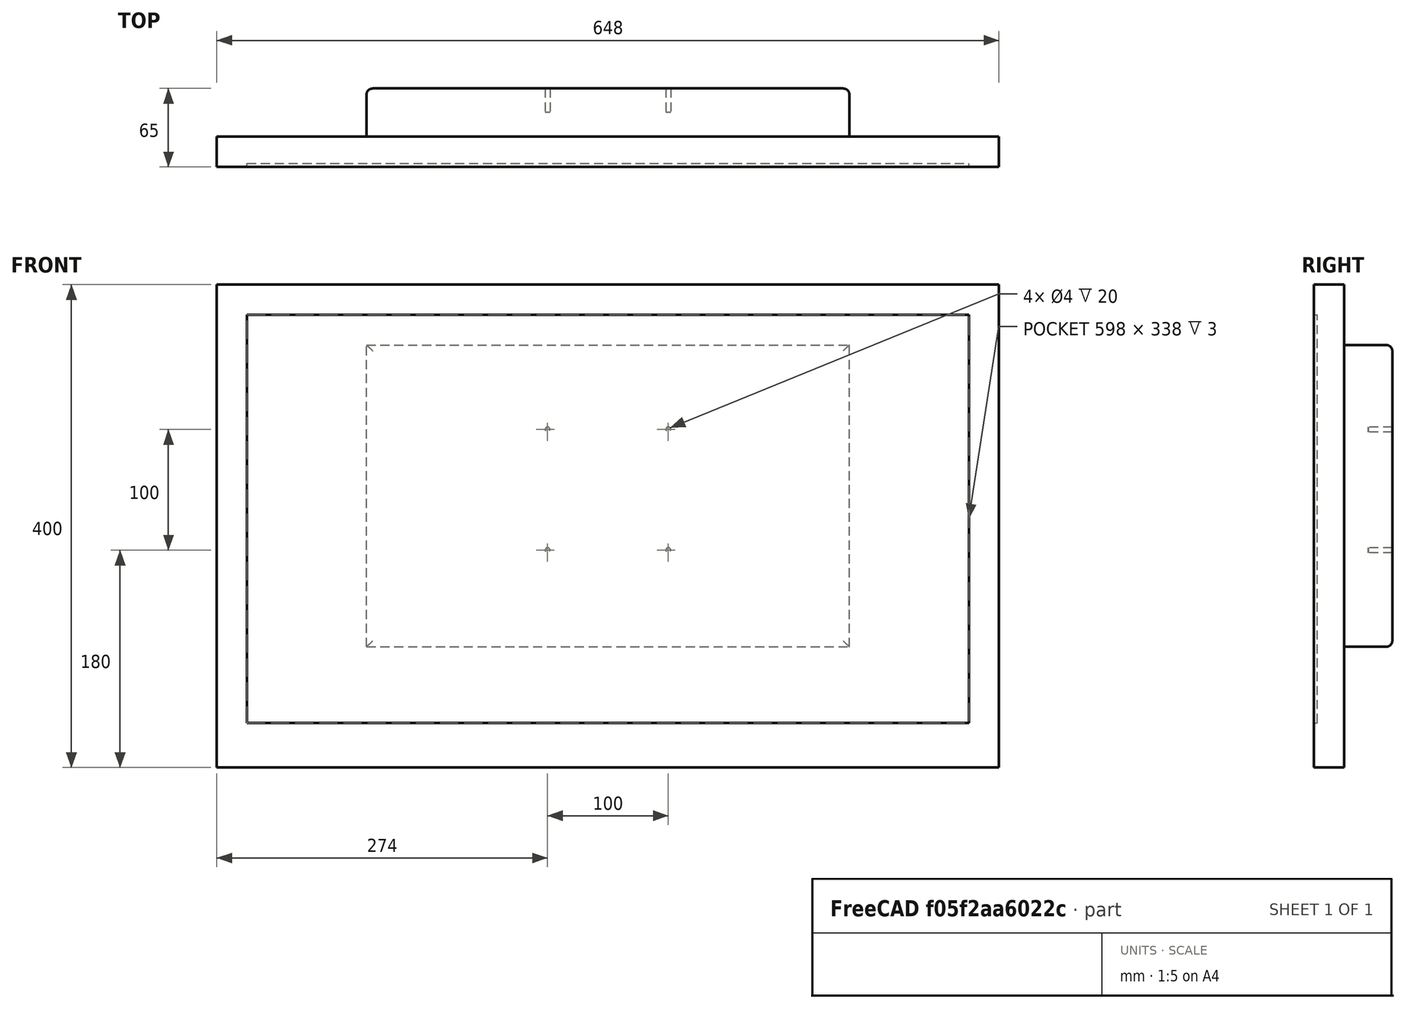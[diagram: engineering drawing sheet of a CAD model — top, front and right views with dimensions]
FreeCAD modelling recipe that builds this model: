
FCSTD DOCUMENT  (FreeCAD 0.14R3402 (Git))
Label: screen
License: CC-BY 3.0
LicenseURL: http://creativecommons.org/licenses/by/3.0/
objects: Part::Cylinder×4, Part::Box×3, Part::Cut×2, App::DocumentObjectGroup×1, Part::MultiFuse×1, PartDesign::Fillet×1
note: 11 computed .brp shape members not serialized (recipe doc carries the construction recipe); baked Part::Feature solids carry a one-line shape summary decoded from their .brp

FEATURE [Part::Box] Box  label="Cube"
  Height = 400
  Length = 648
  Placement = pos=(-324,0,0) rot=(0,0,1;0rad)
  Width = 25
FEATURE [Part::Box] Box001  label="Screen section"
  Height = 338
  Length = 598
  Placement = pos=(-299,-2,37) rot=(0,0,1;0rad)
  Width = 5
FEATURE [Part::Cut] Cut  label="Front"
  Base = -> Box
  Tool = -> Box001
FEATURE [Part::Cylinder] Cylinder
  Angle = 360
  Height = 20
  Placement = pos=(50,65,180) rot=(1,0,0;1.5708rad)
  Radius = 2
FEATURE [Part::Cylinder] Cylinder001
  Angle = 360
  Height = 20
  Placement = pos=(-50,65,180) rot=(1,0,0;1.5708rad)
  Radius = 2
FEATURE [Part::Cylinder] Cylinder002
  Angle = 360
  Height = 20
  Placement = pos=(50,65,280) rot=(1,0,0;1.5708rad)
  Radius = 2
FEATURE [Part::Cylinder] Cylinder003
  Angle = 360
  Height = 20
  Placement = pos=(-50,65,280) rot=(1,0,0;1.5708rad)
  Radius = 2
FEATURE [App::DocumentObjectGroup] Group
  Group = -> [Cylinder001,Cylinder002,Cylinder003]
FEATURE [Part::Box] Box002  label="Cube001"
  Height = 250
  Length = 400
  Placement = pos=(-200,25,100) rot=(0,0,1;0rad)
  Width = 40
FEATURE [Part::MultiFuse] Fusion
  Shapes = -> [Cylinder003,Cylinder,Cylinder001,Cylinder002,Box002]
FEATURE [Part::Cut] Cut001
  Base = -> Box002
  Tool = -> Fusion
FEATURE [PartDesign::Fillet] Fillet
  Base = -> Cut001 [Edge8,Edge3,Edge10,Edge11]
  Radius = 5
